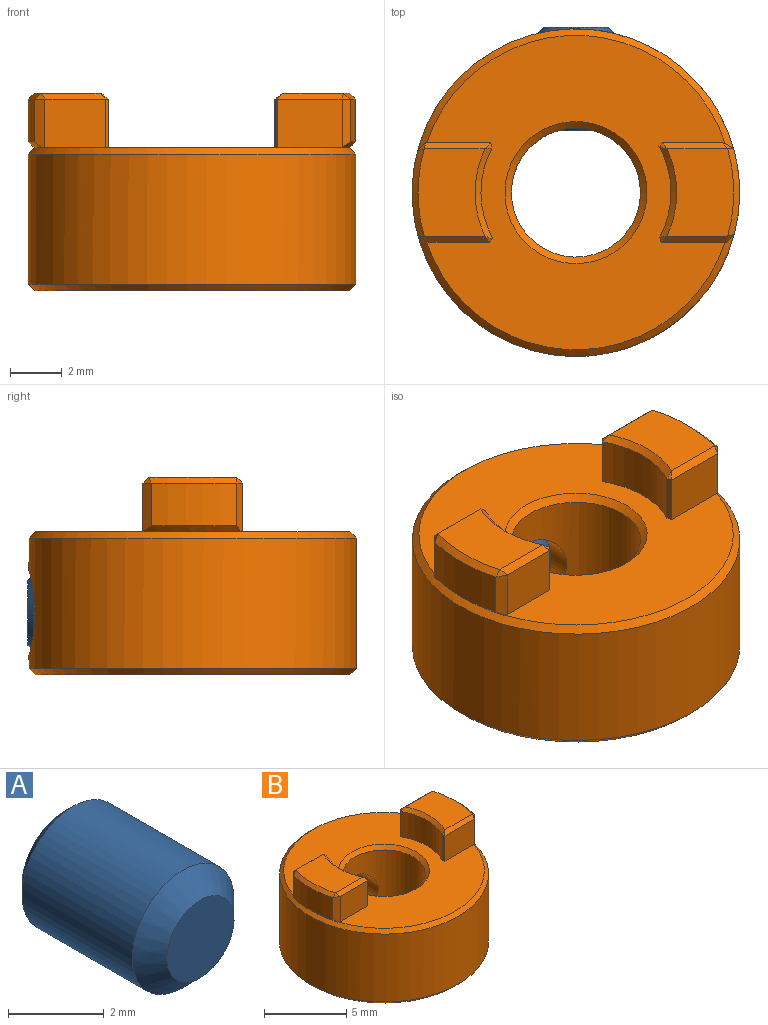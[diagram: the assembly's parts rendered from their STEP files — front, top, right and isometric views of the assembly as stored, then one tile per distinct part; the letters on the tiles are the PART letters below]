
ASSEMBLY  parts=2 mates=1
PART A: 18 faces, bbox 3x4x3 mm
  f0: cylinder r=1.5mm len=3.25mm, axis (0,1,0), area 30.6mm2, adj f16,f17
  f1: plane 1.98x1.98mm, normal (0,-1,0), area 3.1mm2, adj f17
  f2: plane 2.52x2.52mm, normal (0,1,0), area 2.6mm2, adj f3,f4,f5,f6,f7,f8,f16
  f3: cone r=0.87mm half-angle=45deg, axis (0,1,0), area 0.1mm2, adj f2,f10
  f4: cone r=0.87mm half-angle=45deg, axis (0,1,0), area 0.1mm2, adj f2,f11
  f5: cone r=0.87mm half-angle=45deg, axis (0,1,0), area 0.1mm2, adj f2,f12
  f6: cone r=0.87mm half-angle=45deg, axis (0,1,0), area 0.1mm2, adj f2,f13
  f7: cone r=0.87mm half-angle=45deg, axis (0,1,0), area 0.1mm2, adj f2,f14
  f8: cone r=0.87mm half-angle=45deg, axis (0,1,0), area 0.1mm2, adj f2,f15
  f9: plane 1.73x1.5mm, normal (0,1,0), area 1.9mm2, adj f10,f11,f12,f13,f14,f15
  f10: plane 0.9x0.75mm, normal (-0.87,0,-0.5), area 0.7mm2, adj f3,f9,f11,f15
  f11: plane 0.9x0.75mm, normal (-0.87,0,0.5), area 0.7mm2, adj f4,f9,f10,f12
  f12: plane 0.9x0.87mm, normal (0,0,1), area 0.7mm2, adj f5,f9,f11,f13
  f13: plane 0.9x0.75mm, normal (0.87,0,0.5), area 0.7mm2, adj f6,f9,f12,f14
  f14: plane 0.9x0.75mm, normal (0.87,0,-0.5), area 0.7mm2, adj f7,f9,f13,f15
  f15: plane 0.9x0.87mm, normal (0,0,-1), area 0.7mm2, adj f8,f9,f10,f14
  f16: cone r=1.26mm half-angle=45deg, axis (0,-1,0), area 2.9mm2, adj f0,f2
  f17: cone r=1.5mm half-angle=45deg, axis (0,1,0), area 5.6mm2, adj f0,f1
PART B: 48 faces, bbox 12.7x12.7x7.7 mm
  f0: cylinder r=6.35mm len=12.7mm, axis (0,0,1), area 192.5mm2, adj f4,f5,f45
  f1: cylinder r=2.5mm len=5.05mm, axis (0,0,1), area 71.9mm2, adj f44,f46,f47
  f2: plane 12.19x11.6mm, normal (0,0,1), area 73.8mm2, adj f4,f7,f8,f10,f14,f18,f21,f25
  f3: plane 12.19x12.19mm, normal (0,0,-1), area 92.9mm2, adj f5,f46
  f4: cone r=6.1mm half-angle=45deg, axis (0,0,-1), area 14mm2, adj f0,f2,f6,f27
  f5: cone r=6.35mm half-angle=45deg, axis (0,0,1), area 14mm2, adj f0,f3
  f6: plane 3.81x0.34mm, normal (0,0,-1), area 0.1mm2, adj f4,f8,f15,f18
  f7: cylinder r=3.68mm len=3.51mm, axis (0,0,-1), area 6.9mm2, adj f2,f14,f20,f21
  f8: plane 2.52x1.88mm, normal (0,-1,0), area 4.7mm2, adj f2,f6,f12,f13,f14,f15
  f9: cylinder r=6.35mm len=3.32mm, axis (0,0,-1), area 5.6mm2, adj f12,f15,f18,f19
  f10: plane 2.33x1.88mm, normal (0,1,0), area 4.4mm2, adj f2,f18,f21,f24
  f11: plane 3.4x2.6mm, normal (0,0,1), area 7.7mm2, adj f13,f19,f20,f24
  f12: plane 1.88x0.33mm, normal (0.71,-0.71,0), area 0.8mm2, adj f8,f9,f15,f16
  f13: plane 2.58x0.23mm, normal (0,-0.71,0.71), area 0.8mm2, adj f8,f11,f16,f17
  f14: plane 1.88x0.21mm, normal (-0.97,-0.23,0), area 0.4mm2, adj f2,f7,f8,f17
  f15: cone r=6.35mm half-angle=45deg, axis (0,0,1), area 1.2mm2, adj f6,f8,f9,f12,f18
  f16: plane 0.33x0.33mm, normal (0.63,-0.63,0.46), area 0.1mm2, adj f12,f13,f19
  f17: plane 0.27x0.23mm, normal (-0.63,-0.15,0.76), area 0mm2, adj f13,f14,f20
  f18: plane 1.88x0.42mm, normal (0.46,0.89,0), area 0.8mm2, adj f2,f6,f9,f10,f15,f22
  f19: cone r=6.12mm half-angle=45deg, axis (0,0,-1), area 1.1mm2, adj f9,f11,f16,f22
  f20: cone r=3.91mm half-angle=45deg, axis (0,0,1), area 1.2mm2, adj f7,f11,f17,f23
  f21: plane 1.88x0.14mm, normal (-0.71,0.71,0), area 0.4mm2, adj f2,f7,f10,f23
  f22: plane 0.42x0.23mm, normal (0.41,0.79,0.46), area 0.1mm2, adj f18,f19,f24
  f23: plane 0.31x0.23mm, normal (-0.45,0.45,0.77), area 0mm2, adj f20,f21,f24
  f24: plane 2.52x0.23mm, normal (0,0.71,0.71), area 0.8mm2, adj f10,f11,f22,f23
  f25: cylinder r=3.68mm len=3.51mm, axis (0,0,-1), area 6.9mm2, adj f2,f38,f40,f41
  f26: plane 2.33x1.88mm, normal (0,-1,0), area 4.4mm2, adj f2,f34,f41,f43
  f27: plane 3.81x0.34mm, normal (0,0,-1), area 0.1mm2, adj f4,f28,f33,f34
  f28: plane 2.52x1.88mm, normal (0,1,0), area 4.7mm2, adj f2,f27,f32,f33,f37,f38
  f29: cylinder r=6.35mm len=3.32mm, axis (0,0,-1), area 5.6mm2, adj f32,f33,f34,f36
  f30: plane 3.4x2.6mm, normal (0,0,1), area 7.7mm2, adj f36,f37,f40,f43
  f31: plane 0.33x0.33mm, normal (-0.63,0.63,0.46), area 0.1mm2, adj f32,f36,f37
  f32: plane 1.88x0.33mm, normal (-0.71,0.71,0), area 0.8mm2, adj f28,f29,f31,f33
  f33: cone r=6.35mm half-angle=45deg, axis (0,0,1), area 1.2mm2, adj f27,f28,f29,f32,f34
  f34: plane 1.88x0.42mm, normal (-0.46,-0.89,0), area 0.8mm2, adj f2,f26,f27,f29,f33,f35
  f35: plane 0.42x0.23mm, normal (-0.41,-0.79,0.46), area 0.1mm2, adj f34,f36,f43
  f36: cone r=6.12mm half-angle=45deg, axis (0,0,-1), area 1.1mm2, adj f29,f30,f31,f35
  f37: plane 2.58x0.23mm, normal (0,0.71,0.71), area 0.8mm2, adj f28,f30,f31,f39
  f38: plane 1.88x0.21mm, normal (0.97,0.23,0), area 0.4mm2, adj f2,f25,f28,f39
  f39: plane 0.27x0.23mm, normal (0.63,0.15,0.76), area 0mm2, adj f37,f38,f40
  f40: cone r=3.91mm half-angle=45deg, axis (0,0,1), area 1.2mm2, adj f25,f30,f39,f42
  f41: plane 1.88x0.14mm, normal (0.71,-0.71,0), area 0.4mm2, adj f2,f25,f26,f42
  f42: plane 0.31x0.23mm, normal (0.45,-0.45,0.77), area 0mm2, adj f40,f41,f43
  f43: plane 2.52x0.23mm, normal (0,-0.71,0.71), area 0.8mm2, adj f26,f30,f35,f42
  f44: cylinder r=1.5mm len=3.64mm, axis (0,-1,0), area 34.3mm2, adj f1,f45
  f45: bspline ~3.4x3.29mm, area 2.7mm2, adj f0,f44
  f46: cone r=2.75mm half-angle=45deg, axis (0,0,-1), area 5.9mm2, adj f1,f3
  f47: cone r=2.5mm half-angle=45deg, axis (0,0,1), area 5.9mm2, adj f1,f2
PLACE A t=(0.51,-0.98,2.12)mm
PLACE B t=(0.51,-1.03,2.12)mm
MATE fastened A.f0 <-> B.f44  axis (0,1,0) through (0.51,5.13,-3.41)mm
